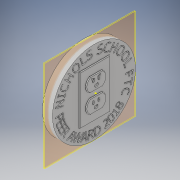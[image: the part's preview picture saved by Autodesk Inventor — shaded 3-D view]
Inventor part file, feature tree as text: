
AUTODESK INVENTOR PART (.ipt)
format: ipt  version: 2018 (Build 220112000, 112)  size: 2,031,616 bytes
history: native  units: in
note: dims shown in document units (in); Inventor stores cm internally (conversion verified against a paired STEP export)
features: fillet x176, sketch x21, extrude x15, plane x2, projected_geometry x1
ambient origin geometry x8: Origin, YZ Plane, XZ Plane, XY Plane, X Axis, Y Axis, Z Axis, Center Point
bodies: Solid1 (feature_tree)
feature tree (215):
  extrude  "Extrusion1"  Depth=0.1in TaperAngle=0.0deg
  extrude  "Extrusion2"  Depth=0.1in
  extrude  "Extrusion3"  Depth=0.8in
  plane  "Work Plane1"
  extrude  "Extrusion4"  Depth=0.932in
  sketch  "Sketch5"  dims[d11=1.4in d12=120.0deg]
  extrude  "Extrusion5"  TaperAngle=120.0deg  [1 undecoded]
  sketch  "Sketch7"  dims[d13=120.0deg d14=0.8686in]
  sketch  "Sketch8"  dims[d15=1.2in d16=1.2in]
  extrude  "Extrusion6"  Depth=0.8686in
  extrude  "Extrusion7"  Depth=1.2in
  sketch  "Sketch9"  dims[d17=0.9315in d18=1.4in]
  extrude  "Extrusion8"  Depth=1.4in
  sketch  "Sketch11"  dims[d23=0.9315in d24=1.5in]
  sketch  "Sketch12"  dims[d26=1.4in d28=0.8in]
  sketch  "Sketch13"  dims[d29=0.1in d30=0.0in d32=1.2in]
  sketch  "Sketch14"  dims[d33=0.808in d34=0.808in]
  sketch  "Sketch15"  dims[d35=120.0deg d36=1.3995in]
  sketch  "Sketch16"  dims[d37=1.4in d38=0.808in d39=0.808in d40=0.1in d41=0.0in d42=4.075in d43=1.4in d44=1.2in d45=1.2in d46=0.18in d47=0.325in d48=0.325in d49=0.18in d50=1.135in d51=1.135in d52=0.1in d53=0.0in d54=0.1in d55=0.0in d56=2.6251in d57=2.625in d58=0.8681in d59=0.1in d60=0.0in d66=0.35in d67=0.1872in d68=0.15in d69=0.35in d70=0.15in d71=0.0487in d72=0.1214in d73=0.1879in d74=0.5745in d75=0.6136in d76=0.1in d77=0.0in d78=0.1in d79=0.0in d80=0.1in d81=0.0in d82=0.1in d83=0.0in d85=0.1in d86=0.0in d87=0.1in d88=0.0in d89=0.1in d90=0.0in d91=0.0625in d92=0.0625in d93=0.0625in d94=0.053in d95=0.053in d96=0.053in d97=0.053in d98=0.053in d99=0.053in d100=0.053in d101=0.053in d102=0.053in d103=0.053in d104=0.053in d105=0.053in d106=0.053in d107=0.053in d108=0.053in d109=0.053in d110=0.053in d111=0.053in d112=0.053in d113=0.053in d114=0.053in d115=0.053in d116=0.053in d117=0.053in d118=0.053in d119=0.053in d120=0.053in d121=0.053in d122=0.053in d123=0.053in d124=0.053in d125=0.053in d126=0.053in d127=0.053in d128=0.053in d129=0.053in d130=0.053in d131=0.053in d132=0.053in d133=0.053in d134=0.053in d135=0.053in d136=0.053in d137=0.053in d138=0.053in d139=0.053in d140=0.053in d141=0.053in d142=0.053in d143=0.053in d144=0.053in d145=0.053in d146=0.053in d147=0.053in d148=0.053in d149=0.053in d150=0.055in d151=0.055in d152=0.055in d153=0.055in d154=0.055in d155=0.055in d156=0.055in d157=0.055in d158=0.055in d159=0.055in d160=0.055in d161=0.055in d162=0.055in d163=0.055in d164=0.055in d165=0.055in d166=0.055in d167=0.055in d168=0.055in d169=0.055in d170=0.055in d171=0.055in d172=0.055in d173=0.055in d174=0.055in d175=0.055in d176=0.055in d177=0.055in d178=0.055in d179=0.055in d180=0.055in d181=0.055in d182=0.055in d183=0.055in d184=0.055in d185=0.045in d186=0.055in d187=0.055in d188=0.055in d189=0.055in d190=0.055in d191=0.055in d192=0.055in d193=0.055in d194=0.055in d195=0.055in d196=0.055in d197=0.055in d198=0.055in d199=0.055in d200=0.055in d201=0.055in d202=0.055in d203=0.055in d204=0.055in d205=0.055in d206=0.055in d207=0.055in d208=0.045in d209=0.045in d210=0.055in d211=0.055in d212=0.055in d213=0.055in d214=0.055in d215=0.055in d216=0.055in d217=0.055in d218=0.055in d219=0.055in d220=0.055in d221=0.045in d222=0.055in d223=0.055in d224=0.055in d225=0.055in d226=0.055in d227=0.055in d228=0.055in d229=0.055in d230=0.045in d231=0.055in]
  extrude  "Extrusion9"  TaperAngle=120.0deg  [1 undecoded]
  extrude  "Extrusion10"  Depth=1.5in
  extrude  "Extrusion11"  Depth=0.8in
  extrude  "Extrusion12"  Depth=0.1in
  sketch  "Sketch17"  dims[d232=0.055in]
  sketch  "Sketch18"  dims[d233=0.055in]
  extrude  "Extrusion13"  Depth=0.808in
  plane  "Work Plane2"
  sketch  "Sketch19"  dims[d234=0.055in]
  extrude  "Extrusion14"  Depth=1.3995in
  sketch  "Sketch21"  dims[d236=0.055in]
  extrude  "Extrusion15"  Depth=0.0625in
  fillet  "Fillet1"  Radius=0.808in
  fillet  "Fillet2"  Radius=0.1in
  fillet  "Fillet3"  Radius=4.075in
  fillet  "Fillet4"  Radius=1.4in
  fillet  "Fillet5"  Radius=1.2in
  fillet  "Fillet6"  Radius=1.2in
  fillet  "Fillet7"  Radius=0.18in
  fillet  "Fillet8"  Radius=0.325in
  fillet  "Fillet9"  Radius=0.325in
  fillet  "Fillet10"  Radius=0.18in
  fillet  "Fillet11"  Radius=1.135in
  fillet  "Fillet12"  Radius=1.135in
  fillet  "Fillet13"  Radius=0.1in
  fillet  "Fillet14"  Radius=0.1in
  fillet  "Fillet15"  Radius=2.6251in
  fillet  "Fillet16"  Radius=2.625in
  fillet  "Fillet17"  Radius=0.8681in
  fillet  "Fillet18"  Radius=0.1in
  fillet  "Fillet19"  Radius=0.35in
  fillet  "Fillet20"  Radius=0.1872in
  fillet  "Fillet21"  Radius=0.15in
  fillet  "Fillet22"  Radius=0.35in
  fillet  "Fillet23"  Radius=0.15in
  fillet  "Fillet24"  Radius=0.0487in
  fillet  "Fillet25"  Radius=0.1214in
  fillet  "Fillet26"  Radius=0.1879in
  fillet  "Fillet27"  Radius=0.5745in
  fillet  "Fillet28"  Radius=0.6136in
  fillet  "Fillet29"  Radius=0.1in
  fillet  "Fillet30"  Radius=0.1in
  fillet  "Fillet31"  Radius=0.1in
  fillet  "Fillet32"  Radius=0.1in
  fillet  "Fillet33"  Radius=0.1in
  fillet  "Fillet34"  Radius=0.1in
  fillet  "Fillet35"  Radius=0.1in
  fillet  "Fillet36"  Radius=0.0625in
  fillet  "Fillet37"  Radius=0.0625in
  fillet  "Fillet38"  Radius=0.0625in
  fillet  "Fillet39"  Radius=0.053in
  fillet  "Fillet40"  Radius=0.053in
  fillet  "Fillet41"  Radius=0.053in
  fillet  "Fillet42"  Radius=0.053in
  fillet  "Fillet43"  Radius=0.053in
  fillet  "Fillet44"  Radius=0.053in
  fillet  "Fillet45"  Radius=0.053in
  fillet  "Fillet46"  Radius=0.053in
  fillet  "Fillet47"  Radius=0.053in
  fillet  "Fillet48"  Radius=0.053in
  fillet  "Fillet49"  Radius=0.053in
  fillet  "Fillet50"  Radius=0.053in
  fillet  "Fillet51"  Radius=0.053in
  fillet  "Fillet52"  Radius=0.053in
  fillet  "Fillet53"  Radius=0.053in
  fillet  "Fillet54"  Radius=0.053in
  fillet  "Fillet55"  Radius=0.053in
  fillet  "Fillet56"  Radius=0.053in
  fillet  "Fillet57"  Radius=0.053in
  fillet  "Fillet58"  Radius=0.053in
  fillet  "Fillet59"  Radius=0.053in
  fillet  "Fillet60"  Radius=0.053in
  fillet  "Fillet61"  Radius=0.053in
  fillet  "Fillet62"  Radius=0.053in
  fillet  "Fillet63"  Radius=0.053in
  fillet  "Fillet64"  Radius=0.053in
  fillet  "Fillet65"  Radius=0.053in
  fillet  "Fillet66"  Radius=0.053in
  fillet  "Fillet67"  Radius=0.053in
  fillet  "Fillet68"  Radius=0.053in
  fillet  "Fillet69"  Radius=0.053in
  fillet  "Fillet70"  Radius=0.053in
  fillet  "Fillet71"  Radius=0.053in
  fillet  "Fillet72"  Radius=0.053in
  fillet  "Fillet73"  Radius=0.053in
  fillet  "Fillet74"  Radius=0.053in
  fillet  "Fillet75"  Radius=0.053in
  fillet  "Fillet76"  Radius=0.053in
  fillet  "Fillet77"  Radius=0.053in
  fillet  "Fillet78"  Radius=0.053in
  fillet  "Fillet79"  Radius=0.053in
  fillet  "Fillet80"  Radius=0.053in
  fillet  "Fillet81"  Radius=0.053in
  fillet  "Fillet82"  Radius=0.053in
  fillet  "Fillet83"  Radius=0.053in
  fillet  "Fillet84"  Radius=0.053in
  fillet  "Fillet85"  Radius=0.053in
  fillet  "Fillet86"  Radius=0.053in
  fillet  "Fillet87"  Radius=0.053in
  fillet  "Fillet88"  Radius=0.053in
  fillet  "Fillet89"  Radius=0.053in
  fillet  "Fillet90"  Radius=0.053in
  fillet  "Fillet91"  Radius=0.053in
  fillet  "Fillet92"  Radius=0.053in
  fillet  "Fillet93"  Radius=0.053in
  fillet  "Fillet94"  Radius=0.053in
  fillet  "Fillet95"  Radius=0.055in
  fillet  "Fillet96"  Radius=0.055in
  fillet  "Fillet97"  Radius=0.055in
  fillet  "Fillet98"  Radius=0.055in
  fillet  "Fillet99"  Radius=0.055in
  fillet  "Fillet100"  Radius=0.055in
  fillet  "Fillet101"  Radius=0.055in
  fillet  "Fillet102"  Radius=0.055in
  fillet  "Fillet103"  Radius=0.055in
  fillet  "Fillet104"  Radius=0.055in
  fillet  "Fillet105"  Radius=0.055in
  fillet  "Fillet106"  Radius=0.055in
  fillet  "Fillet107"  Radius=0.055in
  fillet  "Fillet108"  Radius=0.055in
  fillet  "Fillet109"  Radius=0.055in
  fillet  "Fillet110"  Radius=0.055in
  fillet  "Fillet111"  Radius=0.055in
  fillet  "Fillet112"  Radius=0.055in
  fillet  "Fillet113"  Radius=0.055in
  fillet  "Fillet114"  Radius=0.055in
  fillet  "Fillet115"  Radius=0.055in
  fillet  "Fillet116"  Radius=0.055in
  fillet  "Fillet117"  Radius=0.055in
  fillet  "Fillet118"  Radius=0.055in
  fillet  "Fillet119"  Radius=0.055in
  fillet  "Fillet120"  Radius=0.055in
  fillet  "Fillet121"  Radius=0.055in
  fillet  "Fillet122"  Radius=0.055in
  fillet  "Fillet123"  Radius=0.055in
  fillet  "Fillet124"  Radius=0.055in
  fillet  "Fillet125"  Radius=0.055in
  fillet  "Fillet126"  Radius=0.055in
  fillet  "Fillet127"  Radius=0.055in
  fillet  "Fillet128"  Radius=0.055in
  fillet  "Fillet129"  Radius=0.055in
  fillet  "Fillet130"  Radius=0.045in
  fillet  "Fillet131"  Radius=0.055in
  fillet  "Fillet132"  Radius=0.055in
  fillet  "Fillet133"  Radius=0.055in
  fillet  "Fillet134"  Radius=0.055in
  fillet  "Fillet135"  Radius=0.055in
  fillet  "Fillet136"  Radius=0.055in
  fillet  "Fillet137"  Radius=0.055in
  fillet  "Fillet138"  Radius=0.055in
  fillet  "Fillet139"  Radius=0.055in
  fillet  "Fillet140"  Radius=0.055in
  fillet  "Fillet141"  Radius=0.055in
  fillet  "Fillet142"  Radius=0.055in
  fillet  "Fillet143"  Radius=0.055in
  fillet  "Fillet144"  Radius=0.055in
  fillet  "Fillet145"  Radius=0.055in
  fillet  "Fillet146"  Radius=0.055in
  fillet  "Fillet147"  Radius=0.055in
  fillet  "Fillet148"  Radius=0.055in
  fillet  "Fillet149"  Radius=0.055in
  fillet  "Fillet150"  Radius=0.055in
  fillet  "Fillet151"  Radius=0.055in
  fillet  "Fillet152"  Radius=0.055in
  fillet  "Fillet153"  Radius=0.045in
  fillet  "Fillet154"  Radius=0.045in
  fillet  "Fillet155"  Radius=0.055in
  fillet  "Fillet156"  Radius=0.055in
  fillet  "Fillet157"  Radius=0.055in
  fillet  "Fillet158"  Radius=0.055in
  fillet  "Fillet159"  Radius=0.055in
  fillet  "Fillet160"  Radius=0.055in
  fillet  "Fillet161"  Radius=0.055in
  fillet  "Fillet162"  Radius=0.055in
  fillet  "Fillet163"  Radius=0.055in
  fillet  "Fillet164"  Radius=0.055in
  fillet  "Fillet165"  Radius=0.055in
  fillet  "Fillet166"  Radius=0.045in
  fillet  "Fillet167"  Radius=0.055in
  fillet  "Fillet168"  Radius=0.055in
  fillet  "Fillet169"  Radius=0.055in
  fillet  "Fillet170"  Radius=0.055in
  fillet  "Fillet171"  Radius=0.055in
  fillet  "Fillet172"  Radius=0.055in
  fillet  "Fillet173"  Radius=0.055in
  fillet  "Fillet174"  Radius=0.055in
  fillet  "Fillet175"  Radius=0.045in
  fillet  "Fillet176"  Radius=0.055in
  sketch  "Sketch1"  dims[d0=1.0in d1=0.0in d2=0.1in d3=0.0in]
  sketch  "Sketch2"  dims[d4=0.1in d5=0.0in d6=1.2in]
  sketch  "Sketch3"  dims[d7=1.2in d8=0.8in]
  projected_geometry  "Projected Loop1"
  sketch  "Sketch4"  dims[d9=0.9315in d10=0.932in]
  sketch  "Sketch10"  dims[d21=120.0deg d22=120.0deg]
  sketch  "Sketch20"  dims[d235=0.045in]
  sketch  "Sketch22"  dims[d237=0.055in d238=0.055in d239=0.055in d240=0.055in d241=0.055in d242=0.055in d243=0.055in d244=0.055in d245=0.055in d246=0.055in d247=0.055in d248=0.055in d249=0.055in d250=0.055in d251=0.055in d252=0.055in d253=0.055in d254=0.038in d255=0.038in d256=0.055in d257=0.038in d258=0.055in d259=0.038in d260=0.055in d261=0.055in d262=0.055in d263=0.055in d264=0.0625in d265=0.0625in d266=0.0625in]
note: 2 required parameter values undecoded (feature->parameter linkage not recoverable at this tier; creation-order binding heuristic only, values carry confidence <= 0.55)
